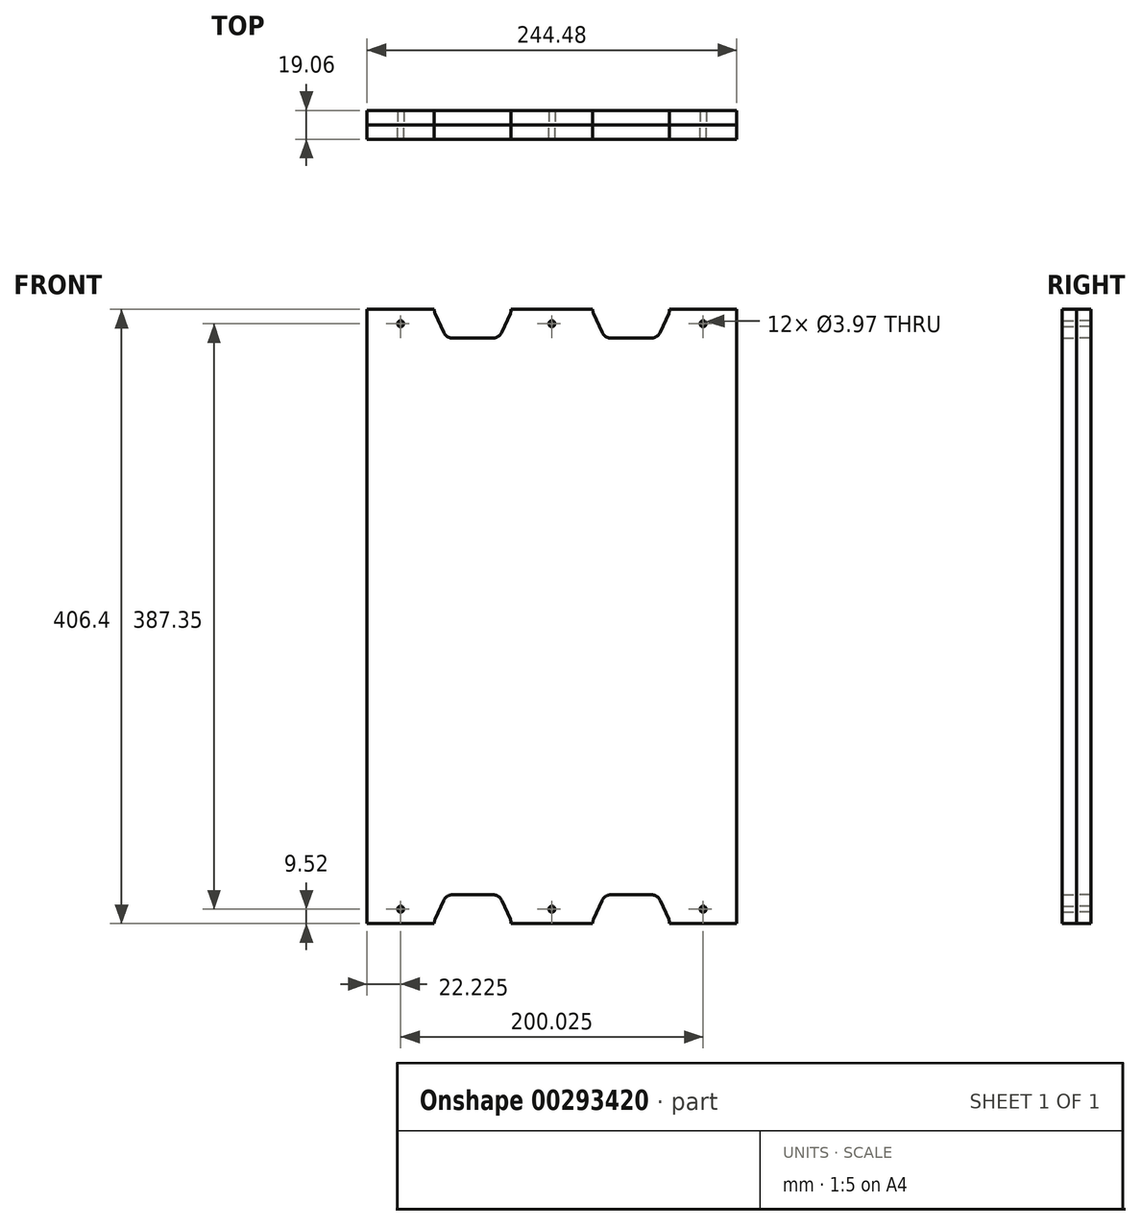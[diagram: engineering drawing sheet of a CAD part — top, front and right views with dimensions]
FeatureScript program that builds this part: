
annotation { "Feature Type Name" : "Feature", "Feature Type Description" : "" }
export const myFeature = defineFeature(function(context is Context, id is Id, definition is map)
    precondition{}
    {
        {
            var Q0;
            Q0=qCreatedBy(makeId("Front.planeOp"),FACE);
            var sketch = newSketch(context, id + "F0", { "sketchPlane" : qUnion([Q0])});
            skLineSegment(sketch, "E0", {"start": v(-121.86, 189.42) * mm, "end": v(122.62, 189.42) * mm});
            skLineSegment(sketch, "E1", {"start": v(122.62, -216.98) * mm, "end": v(-121.86, -216.98) * mm});
            skLineSegment(sketch, "E2", {"start": v(-26.6, -223.33) * mm, "end": v(-26.6, -207.46) * mm, "construction": true});
            skLineSegment(sketch, "E3", {"start": v(-23, -223.34) * mm, "end": v(-37.45, -191.54) * mm, "construction": true});
            skLineSegment(sketch, "E4", {"start": v(-66.57, -191.54) * mm, "end": v(-81.02, -223.33) * mm, "construction": true});
            skLineSegment(sketch, "E5", {"start": v(-26.6, -197.93) * mm, "end": v(-77.4, -197.93) * mm, "construction": true});
            skLineSegment(sketch, "E6", {"start": v(-77.4, -207.46) * mm, "end": v(-77.4, -223.33) * mm, "construction": true});
            skLineSegment(sketch, "E7", {"start": v(-83.76, -215.4) * mm, "end": v(-20.26, -215.4) * mm, "construction": true});
            skLineSegment(sketch, "E8", {"start": v(-20.26, -216.98) * mm, "end": v(-83.76, -216.98) * mm, "construction": true});
            skLineSegment(sketch, "E9", {"start": v(-26.6, -216.98) * mm, "end": v(-26.6, -216.77) * mm});
            skLineSegment(sketch, "E10", {"start": v(-27.18, -214.15) * mm, "end": v(-32.86, -201.66) * mm});
            skLineSegment(sketch, "E11", {"start": v(-38.64, -197.93) * mm, "end": v(-65.38, -197.93) * mm});
            skLineSegment(sketch, "E12", {"start": v(-71.16, -201.66) * mm, "end": v(-76.84, -214.15) * mm});
            skLineSegment(sketch, "E13", {"start": v(-77.4, -216.77) * mm, "end": v(-77.4, -216.98) * mm});
            skPoint(sketch, "E14.visualSharp", {"position": v(-34.55, -197.93) * mm});
            skArc(sketch, "E14.filletArc", {"start": v(-32.86, -201.66) * mm, "mid": v(-35.2, -198.95) * mm, "end": v(-38.64, -197.93) * mm});
            skPoint(sketch, "E15.visualSharp", {"position": v(-69.47, -197.93) * mm});
            skArc(sketch, "E15.filletArc", {"start": v(-65.38, -197.93) * mm, "mid": v(-68.82, -198.95) * mm, "end": v(-71.16, -201.66) * mm});
            skPoint(sketch, "E16.visualSharp", {"position": v(-77.4, -215.4) * mm});
            skArc(sketch, "E16.filletArc", {"start": v(-76.84, -214.15) * mm, "mid": v(-77.27, -215.43) * mm, "end": v(-77.4, -216.77) * mm});
            skPoint(sketch, "E17.visualSharp", {"position": v(-26.6, -215.4) * mm});
            skArc(sketch, "E17.filletArc", {"start": v(-26.6, -216.77) * mm, "mid": v(-26.75, -215.43) * mm, "end": v(-27.18, -214.15) * mm});
            skLineSegment(sketch, "E18", {"start": v(0.38, 189.42) * mm, "end": v(0.38, -216.98) * mm, "construction": true});
            skLineSegment(sketch, "E19.MirrorCS", {"start": v(-83.76, 187.83) * mm, "end": v(-20.26, 187.83) * mm, "construction": true});
            skLineSegment(sketch, "E20.MirrorCS", {"start": v(-20.26, 189.42) * mm, "end": v(-83.76, 189.42) * mm, "construction": true});
            skArc(sketch, "E21.MirrorCS", {"start": v(-26.6, 189.2) * mm, "mid": v(-26.75, 187.86) * mm, "end": v(-27.18, 186.58) * mm});
            skLineSegment(sketch, "E22.MirrorCS", {"start": v(-77.4, 189.2) * mm, "end": v(-77.4, 189.42) * mm});
            skArc(sketch, "E23.MirrorCS", {"start": v(-76.84, 186.58) * mm, "mid": v(-77.27, 187.86) * mm, "end": v(-77.4, 189.2) * mm});
            skLineSegment(sketch, "E24.MirrorCS", {"start": v(-26.6, 189.42) * mm, "end": v(-26.6, 189.2) * mm});
            skLineSegment(sketch, "E25.MirrorCS", {"start": v(-71.16, 174.09) * mm, "end": v(-76.84, 186.58) * mm});
            skArc(sketch, "E26.MirrorCS", {"start": v(-32.86, 174.09) * mm, "mid": v(-35.2, 171.38) * mm, "end": v(-38.64, 170.37) * mm});
            skArc(sketch, "E27.MirrorCS", {"start": v(-65.38, 170.37) * mm, "mid": v(-68.82, 171.38) * mm, "end": v(-71.16, 174.09) * mm});
            skLineSegment(sketch, "E28.MirrorCS", {"start": v(-38.64, 170.37) * mm, "end": v(-65.38, 170.37) * mm});
            skLineSegment(sketch, "E29.MirrorCS", {"start": v(-27.18, 186.58) * mm, "end": v(-32.86, 174.09) * mm});
            skLineSegment(sketch, "E30.MirrorCS", {"start": v(-26.6, 170.37) * mm, "end": v(-77.4, 170.37) * mm, "construction": true});
            skPoint(sketch, "E31.MirrorP", {"position": v(-77.4, 187.83) * mm});
            skPoint(sketch, "E32.MirrorP", {"position": v(-34.55, 170.37) * mm});
            skLineSegment(sketch, "E33.MirrorCS", {"start": v(-77.4, 179.9) * mm, "end": v(-77.4, 195.77) * mm, "construction": true});
            skLineSegment(sketch, "E34.MirrorCS", {"start": v(-23, 195.77) * mm, "end": v(-37.45, 163.97) * mm, "construction": true});
            skLineSegment(sketch, "E35.MirrorCS", {"start": v(-26.6, 195.77) * mm, "end": v(-26.6, 179.9) * mm, "construction": true});
            skLineSegment(sketch, "E36.MirrorCS", {"start": v(-66.57, 163.97) * mm, "end": v(-81.02, 195.77) * mm, "construction": true});
            skPoint(sketch, "E37.MirrorP", {"position": v(-26.6, 187.83) * mm});
            skPoint(sketch, "E38.MirrorP", {"position": v(-69.47, 170.37) * mm});
            skLineSegment(sketch, "E39.MirrorCS", {"start": v(78.17, 189.2) * mm, "end": v(78.17, 189.42) * mm});
            skLineSegment(sketch, "E40.MirrorCS", {"start": v(78.17, -216.77) * mm, "end": v(78.17, -216.98) * mm});
            skLineSegment(sketch, "E41.MirrorCS", {"start": v(27.37, -216.98) * mm, "end": v(27.37, -216.77) * mm});
            skArc(sketch, "E42.MirrorCS", {"start": v(27.37, 189.2) * mm, "mid": v(27.5, 187.86) * mm, "end": v(27.93, 186.58) * mm});
            skLineSegment(sketch, "E43.MirrorCS", {"start": v(27.37, 189.42) * mm, "end": v(27.37, 189.2) * mm});
            skArc(sketch, "E44.MirrorCS", {"start": v(77.6, 186.58) * mm, "mid": v(78.02, 187.86) * mm, "end": v(78.17, 189.2) * mm});
            skArc(sketch, "E45.MirrorCS", {"start": v(27.37, -216.77) * mm, "mid": v(27.5, -215.43) * mm, "end": v(27.93, -214.15) * mm});
            skArc(sketch, "E46.MirrorCS", {"start": v(77.6, -214.15) * mm, "mid": v(78.02, -215.43) * mm, "end": v(78.17, -216.77) * mm});
            skLineSegment(sketch, "E47.MirrorCS", {"start": v(71.92, -201.66) * mm, "end": v(77.6, -214.15) * mm});
            skLineSegment(sketch, "E48.MirrorCS", {"start": v(71.92, 174.09) * mm, "end": v(77.6, 186.58) * mm});
            skLineSegment(sketch, "E49.MirrorCS", {"start": v(27.93, -214.15) * mm, "end": v(33.61, -201.66) * mm});
            skArc(sketch, "E50.MirrorCS", {"start": v(33.61, 174.09) * mm, "mid": v(35.95, 171.38) * mm, "end": v(39.4, 170.37) * mm});
            skArc(sketch, "E51.MirrorCS", {"start": v(66.14, 170.37) * mm, "mid": v(69.58, 171.38) * mm, "end": v(71.92, 174.09) * mm});
            skArc(sketch, "E52.MirrorCS", {"start": v(33.61, -201.66) * mm, "mid": v(35.95, -198.95) * mm, "end": v(39.4, -197.93) * mm});
            skLineSegment(sketch, "E53.MirrorCS", {"start": v(27.93, 186.58) * mm, "end": v(33.61, 174.09) * mm});
            skArc(sketch, "E54.MirrorCS", {"start": v(66.14, -197.93) * mm, "mid": v(69.58, -198.95) * mm, "end": v(71.92, -201.66) * mm});
            skLineSegment(sketch, "E55.MirrorCS", {"start": v(67.32, 163.97) * mm, "end": v(81.77, 195.77) * mm, "construction": true});
            skLineSegment(sketch, "E56.MirrorCS", {"start": v(27.37, 195.77) * mm, "end": v(27.37, 179.9) * mm, "construction": true});
            skLineSegment(sketch, "E57.MirrorCS", {"start": v(78.17, 179.9) * mm, "end": v(78.17, 195.77) * mm, "construction": true});
            skLineSegment(sketch, "E58.MirrorCS", {"start": v(23.76, -223.34) * mm, "end": v(38.2, -191.54) * mm, "construction": true});
            skLineSegment(sketch, "E59.MirrorCS", {"start": v(67.32, -191.54) * mm, "end": v(81.77, -223.33) * mm, "construction": true});
            skLineSegment(sketch, "E60.MirrorCS", {"start": v(39.4, -197.93) * mm, "end": v(66.14, -197.93) * mm});
            skLineSegment(sketch, "E61.MirrorCS", {"start": v(27.37, -223.33) * mm, "end": v(27.37, -207.46) * mm, "construction": true});
            skLineSegment(sketch, "E62.MirrorCS", {"start": v(23.76, 195.77) * mm, "end": v(38.2, 163.97) * mm, "construction": true});
            skLineSegment(sketch, "E63.MirrorCS", {"start": v(39.4, 170.37) * mm, "end": v(66.14, 170.37) * mm});
            skLineSegment(sketch, "E64.MirrorCS", {"start": v(78.17, -207.46) * mm, "end": v(78.17, -223.33) * mm, "construction": true});
            skLineSegment(sketch, "E65.MirrorCS", {"start": v(21.02, -216.98) * mm, "end": v(84.52, -216.98) * mm, "construction": true});
            skPoint(sketch, "E66.MirrorP", {"position": v(78.17, -215.4) * mm});
            skLineSegment(sketch, "E67.MirrorCS", {"start": v(27.37, -197.93) * mm, "end": v(78.17, -197.93) * mm, "construction": true});
            skPoint(sketch, "E68.MirrorP", {"position": v(70.23, -197.93) * mm});
            skLineSegment(sketch, "E69.MirrorCS", {"start": v(27.37, 170.37) * mm, "end": v(78.17, 170.37) * mm, "construction": true});
            skPoint(sketch, "E70.MirrorP", {"position": v(35.3, -197.93) * mm});
            skPoint(sketch, "E71.MirrorP", {"position": v(78.17, 187.83) * mm});
            skPoint(sketch, "E72.MirrorP", {"position": v(35.3, 170.37) * mm});
            skLineSegment(sketch, "E73.MirrorCS", {"start": v(84.52, 187.83) * mm, "end": v(21.02, 187.83) * mm, "construction": true});
            skPoint(sketch, "E74.MirrorP", {"position": v(27.37, -215.4) * mm});
            skPoint(sketch, "E75.MirrorP", {"position": v(27.37, 187.83) * mm});
            skLineSegment(sketch, "E76.MirrorCS", {"start": v(21.02, 189.42) * mm, "end": v(84.52, 189.42) * mm, "construction": true});
            skPoint(sketch, "E77.MirrorP", {"position": v(70.23, 170.37) * mm});
            skLineSegment(sketch, "E78.MirrorCS", {"start": v(84.52, -215.4) * mm, "end": v(21.02, -215.4) * mm, "construction": true});
            skLineSegment(sketch, "E79", {"start": v(122.62, 189.42) * mm, "end": v(122.62, -216.98) * mm});
            skLineSegment(sketch, "E80", {"start": v(-121.86, -216.98) * mm, "end": v(-121.86, 189.42) * mm});
            skCircle(sketch, "E81", {"center": v(100.4, -207.46) * mm, "radius": 1.98 * mm});
            skCircle(sketch, "E82", {"center": v(0.38, -207.46) * mm, "radius": 1.98 * mm});
            skCircle(sketch, "E83", {"center": v(-99.63, -207.46) * mm, "radius": 1.98 * mm});
            skCircle(sketch, "E84", {"center": v(-99.63, 179.9) * mm, "radius": 1.98 * mm});
            skCircle(sketch, "E85", {"center": v(0.38, 179.9) * mm, "radius": 1.98 * mm});
            skCircle(sketch, "E86", {"center": v(100.4, 179.9) * mm, "radius": 1.98 * mm});
            skLineSegment(sketch, "E87", {"start": v(78.17, 170.37) * mm, "end": v(122.62, 170.37) * mm, "construction": true});
            skSolve(sketch);
        }
        {
            var Q0;
            {var subQ5=sQuery(id+"F0.wireOp",EDGE,"E9");Q0=makeQuery(id+"F0.imprint","IMPRINT",FACE,{"disambiguationData":[TD([[makeQuery(id+"F0.imprint","IMPRINT",EDGE,{"derivedFrom":subQ5}),-1.0]])]});}
            extrude(context, id + "F1", {"entities" : qUnion([Q0]), "depth" : 9.52 * mm, "offsetDistance" : 25.4 * mm});
        }
        {
            var Q0;
            {var subQ5=sQuery(id+"F0.wireOp",EDGE,"E9");Q0=makeQuery(id+"F0.imprint","IMPRINT",FACE,{"disambiguationData":[TD([[makeQuery(id+"F0.imprint","IMPRINT",EDGE,{"derivedFrom":subQ5}),-1.0]])]});}
            extrude(context, id + "F2", {"entities" : qUnion([Q0]), "oppositeDirection" : true, "depth" : 9.52 * mm, "offsetDistance" : 25.4 * mm});
        }
    });
